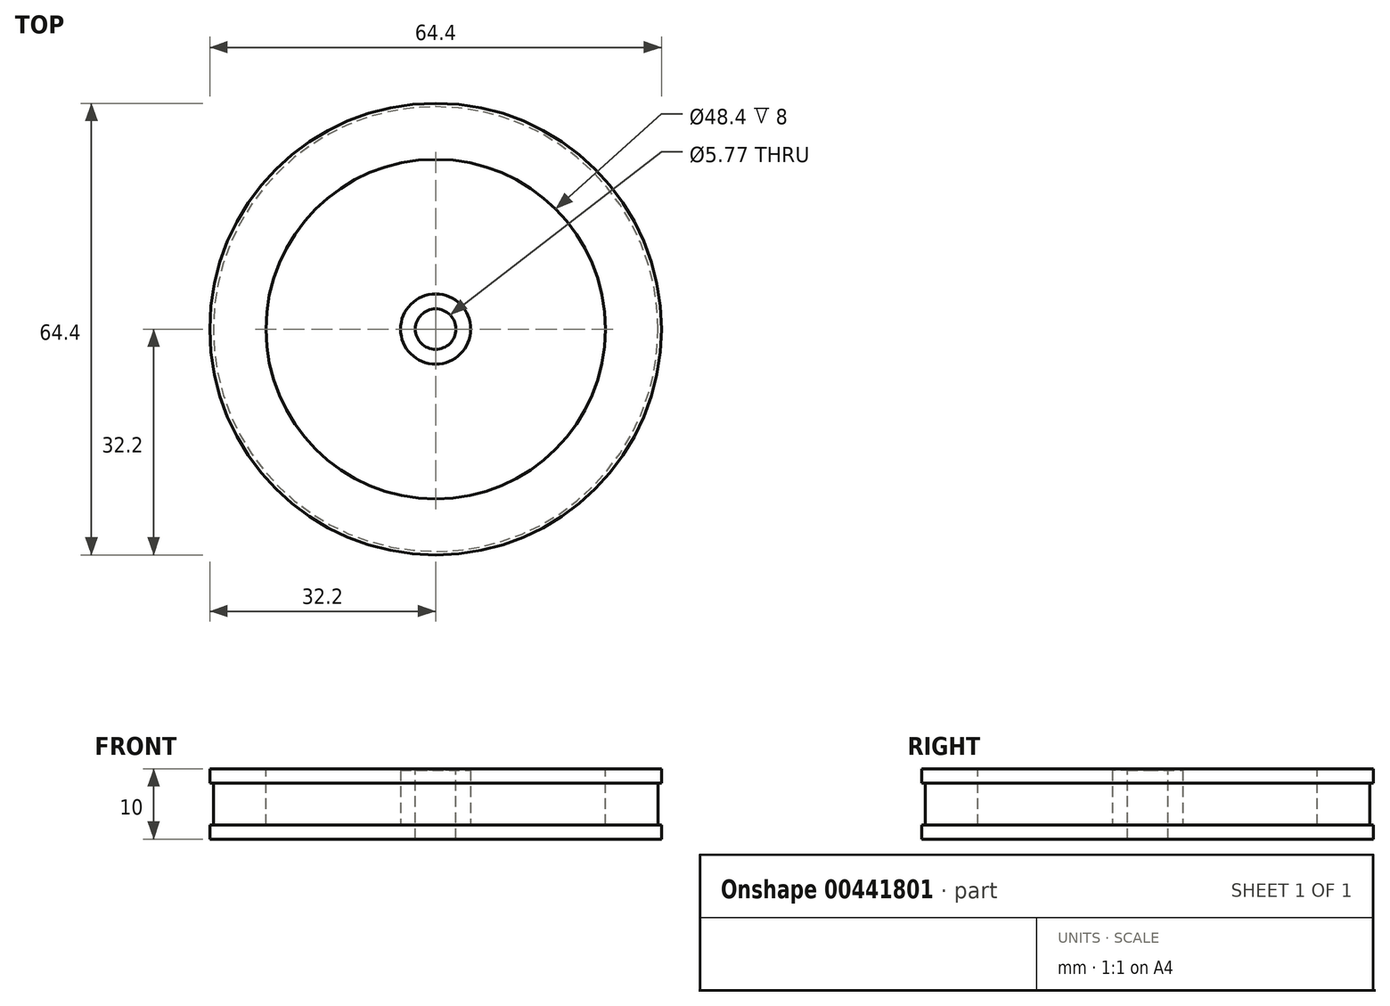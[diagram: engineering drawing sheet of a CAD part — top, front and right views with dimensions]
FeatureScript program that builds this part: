
annotation { "Feature Type Name" : "Feature", "Feature Type Description" : "" }
export const myFeature = defineFeature(function(context is Context, id is Id, definition is map)
    precondition{}
    {
        {
            var Q0;
            Q0=qCreatedBy(makeId("Front.planeOp"),FACE);
            var sketch = newSketch(context, id + "F0", { "sketchPlane" : qUnion([Q0])});
            skLineSegment(sketch, "E0", {"start": v(0, 0) * mm, "end": v(-32.2, 0) * mm});
            skLineSegment(sketch, "E1", {"start": v(-32.2, 0) * mm, "end": v(-32.2, 2) * mm});
            skLineSegment(sketch, "E2", {"start": v(-32.2, 2) * mm, "end": v(-31.7, 2) * mm});
            skLineSegment(sketch, "E3", {"start": v(-31.7, 2) * mm, "end": v(-31.7, 8) * mm});
            skLineSegment(sketch, "E4", {"start": v(-31.7, 8) * mm, "end": v(-32.2, 8) * mm});
            skLineSegment(sketch, "E5", {"start": v(-32.2, 8) * mm, "end": v(-32.2, 10) * mm});
            skLineSegment(sketch, "E6", {"start": v(-32.2, 10) * mm, "end": v(-24.2, 10) * mm});
            skLineSegment(sketch, "E7", {"start": v(-24.2, 10) * mm, "end": v(-24.2, 2) * mm});
            skLineSegment(sketch, "E8", {"start": v(-24.2, 2) * mm, "end": v(0, 2) * mm});
            skLineSegment(sketch, "E9", {"start": v(0, 2) * mm, "end": v(0, 0) * mm});
            skSolve(sketch);
        }
        {
            var Q0;
            Q0=makeQuery(id+"F0.imprint","IMPRINT",FACE,{"disambiguationData":[TD([[makeQuery(id+"F0.imprint","IMPRINT",EDGE,{"derivedFrom":sQuery(id+"F0.wireOp",EDGE,"E0")}),-1.0]])]});
            var Q1;
            Q1=sQuery(id+"F0.wireOp",EDGE,"E9");
            revolve(context, id + "F1", {"entities" : qUnion([Q0]), "axis" : qUnion([Q1]), "revolveType" : RevolveType.FULL});
        }
        {
            var Q0;
            Q0=makeQuery(id+"F1.opRevolve","SWEPT_FACE",FACE,{"disambiguationData":[OSD([sQuery(id+"F0.wireOp",EDGE,"E8")])]});
            var sketch = newSketch(context, id + "F2", { "sketchPlane" : qUnion([Q0])});
            skCircle(sketch, "E10", {"center": v(0, 0) * mm, "radius": 5 * mm});
            skSolve(sketch);
        }
        {
            var Q0;
            Q0=makeQuery(id+"F2.imprint","IMPRINT",FACE,{"disambiguationData":[TD([[makeQuery(id+"F2.imprint","IMPRINT",EDGE,{"derivedFrom":sQuery(id+"F2.wireOp",EDGE,"E10")}),1.0]])]});
            extrude(context, id + "F3", {"entities" : qUnion([Q0]), "operationType" : NewBodyOperationType.ADD, "depth" : 7.8 * mm});
        }
        {
            var Q0;
            Q0=makeQuery(id+"F3.opExtrude","CAP_FACE",FACE,{"disambiguationData":[OSD([sQuery(id+"F2.wireOp",EDGE,"E10")])],"isStart":false});
            var sketch = newSketch(context, id + "F4", { "sketchPlane" : qUnion([Q0])});
            skCircle(sketch, "E11", {"center": v(0, 0) * mm, "radius": 2.89 * mm});
            skSolve(sketch);
        }
        {
            var Q0;
            Q0=makeQuery(id+"F4.imprint","IMPRINT",FACE,{"disambiguationData":[TD([[makeQuery(id+"F4.imprint","IMPRINT",EDGE,{"derivedFrom":sQuery(id+"F4.wireOp",EDGE,"E11")}),1.0]])]});
            extrude(context, id + "F5", {"entities" : qUnion([Q0]), "operationType" : NewBodyOperationType.REMOVE, "oppositeDirection" : true, "depth" : 25 * mm});
        }
    });
